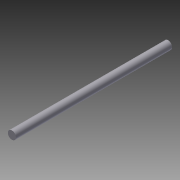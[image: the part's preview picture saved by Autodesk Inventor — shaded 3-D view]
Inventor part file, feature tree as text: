
AUTODESK INVENTOR PART (.ipt)
format: ipt  version: 2011 (Build 150239000, 239)  size: 59,904 bytes
history: native  units: in
note: dims shown in document units (in); Inventor stores cm internally (conversion verified against a paired STEP export)
features: extrude x1, sketch x1
ambient origin geometry x8: Origin, YZ Plane, XZ Plane, XY Plane, X Axis, Y Axis, Z Axis, Center Point
bodies: Solid1 (feature_tree)
feature tree (2):
  extrude  "Extrusion1"  Depth=12.0in TaperAngle=0.0deg
  sketch  "Sketch1"  dims[d0=0.625in d1=12.0in d2=0.0in]
